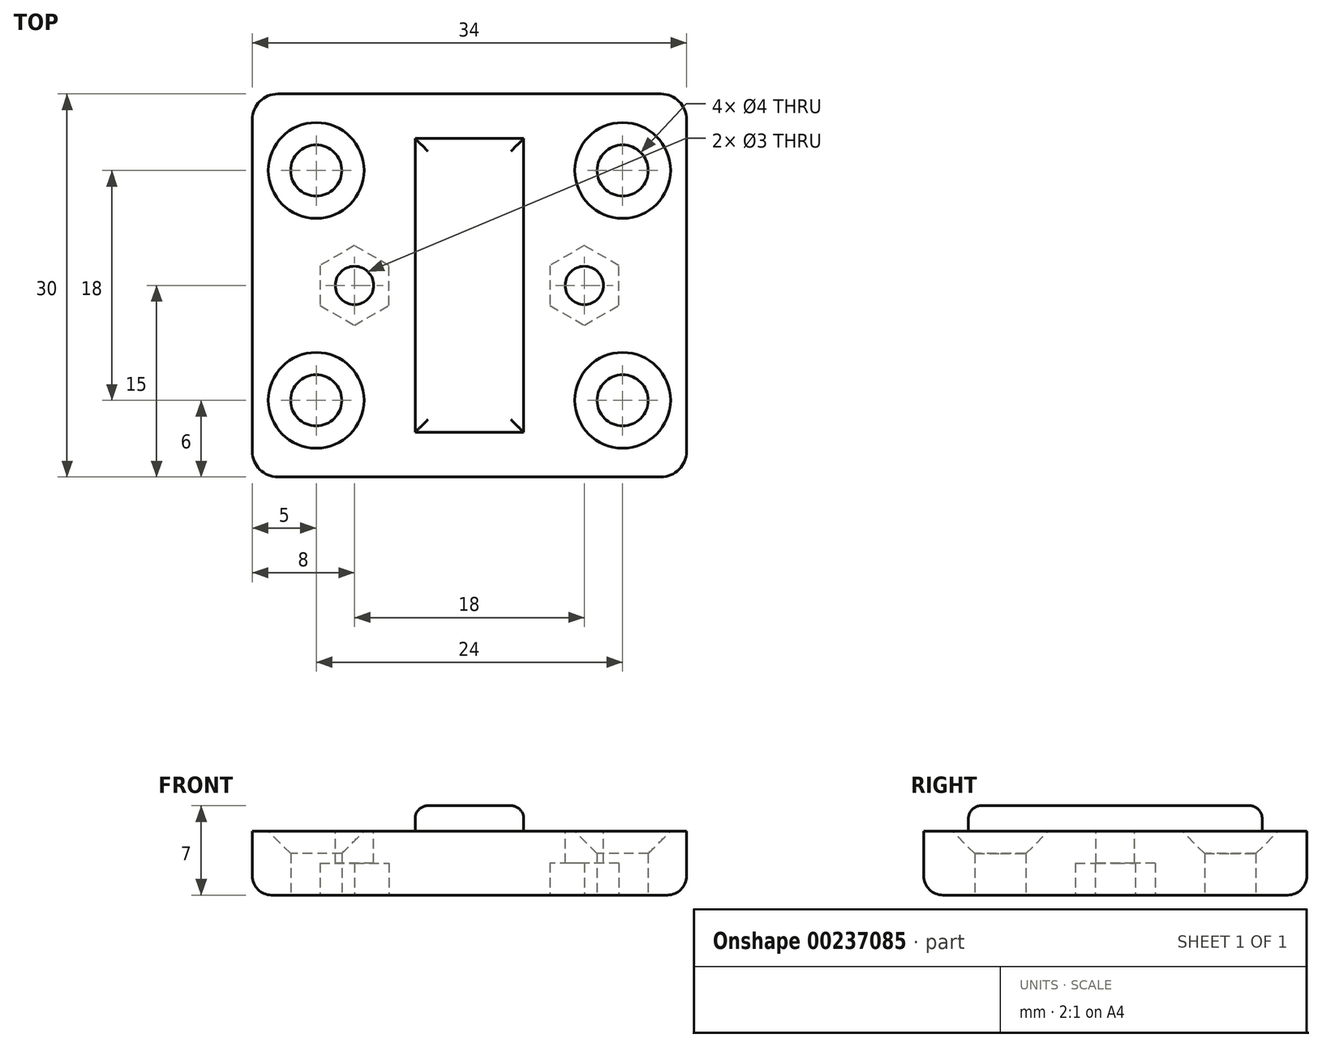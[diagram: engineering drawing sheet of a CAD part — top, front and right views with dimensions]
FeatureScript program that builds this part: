
annotation { "Feature Type Name" : "Feature", "Feature Type Description" : "" }
export const myFeature = defineFeature(function(context is Context, id is Id, definition is map)
    precondition{}
    {
        {
            var Q0;
            Q0=qCreatedBy(makeId("Top.planeOp"),FACE);
            var sketch = newSketch(context, id + "F0", { "sketchPlane" : qUnion([Q0])});
            skLineSegment(sketch, "E0.bottom", {"start": v(-12, 9) * mm, "end": v(12, 9) * mm, "construction": true});
            skLineSegment(sketch, "E0.top", {"start": v(-12, -9) * mm, "end": v(12, -9) * mm, "construction": true});
            skLineSegment(sketch, "E0.left", {"start": v(-12, 9) * mm, "end": v(-12, -9) * mm, "construction": true});
            skLineSegment(sketch, "E0.right", {"start": v(12, 9) * mm, "end": v(12, -9) * mm, "construction": true});
            skCircle(sketch, "E1", {"center": v(-12, 9) * mm, "radius": 2 * mm});
            skCircle(sketch, "E2", {"center": v(12, 9) * mm, "radius": 2 * mm});
            skCircle(sketch, "E3", {"center": v(-12, -9) * mm, "radius": 2 * mm});
            skCircle(sketch, "E4", {"center": v(12, -9) * mm, "radius": 2 * mm});
            skLineSegment(sketch, "E5.bottom", {"start": v(-17, -15) * mm, "end": v(17, -15) * mm});
            skLineSegment(sketch, "E5.top", {"start": v(-17, 15) * mm, "end": v(17, 15) * mm});
            skLineSegment(sketch, "E5.left", {"start": v(-17, -15) * mm, "end": v(-17, 15) * mm});
            skLineSegment(sketch, "E5.right", {"start": v(17, -15) * mm, "end": v(17, 15) * mm});
            skPoint(sketch, "E5.middle", {"position": v(0, 0) * mm});
            skSolve(sketch);
        }
        {
            var Q0;
            Q0=makeQuery(id+"F0.imprint","IMPRINT",FACE,{"disambiguationData":[TD([[makeQuery(id+"F0.imprint","IMPRINT",EDGE,{"derivedFrom":sQuery(id+"F0.wireOp",EDGE,"E1")}),-1.0]])]});
            var Q1;
            Q1=sQuery(id+"F0.wireOp",EDGE,"E0.right");
            var Q2;
            Q2=sQuery(id+"F0.wireOp",EDGE,"E0.bottom");
            var Q3;
            Q3=sQuery(id+"F0.wireOp",EDGE,"E0.left");
            var Q4;
            Q4=sQuery(id+"F0.wireOp",EDGE,"E0.top");
            extrude(context, id + "F1", {"entities" : qUnion([Q0]), "surfaceEntities" : qUnion([Q1, Q2, Q3, Q4]), "depth" : 5 * mm});
        }
        {
            var Q0;
            Q0=makeQuery(id+"F1.opExtrude","CAP_FACE",FACE,{"disambiguationData":[OSD([sQuery(id+"F0.wireOp",EDGE,"E1"),sQuery(id+"F0.wireOp",EDGE,"E2"),sQuery(id+"F0.wireOp",EDGE,"E3"),sQuery(id+"F0.wireOp",EDGE,"E4"),sQuery(id+"F0.wireOp",EDGE,"E5.bottom"),sQuery(id+"F0.wireOp",EDGE,"E5.top"),sQuery(id+"F0.wireOp",EDGE,"E5.left"),sQuery(id+"F0.wireOp",EDGE,"E5.right")])],"isStart":false});
            var sketch = newSketch(context, id + "F2", { "sketchPlane" : qUnion([Q0])});
            skLineSegment(sketch, "E6.bottom", {"start": v(15, 8) * mm, "end": v(9, 8) * mm, "construction": true});
            skLineSegment(sketch, "E6.top", {"start": v(15, -8) * mm, "end": v(9, -8) * mm, "construction": true});
            skLineSegment(sketch, "E6.left", {"start": v(15, 8) * mm, "end": v(15, -8) * mm, "construction": true});
            skLineSegment(sketch, "E6.right", {"start": v(9, 8) * mm, "end": v(9, -8) * mm, "construction": true});
            skCircle(sketch, "E7", {"center": v(15, 8) * mm, "radius": 1.5 * mm});
            skCircle(sketch, "E8", {"center": v(15, -8) * mm, "radius": 1.5 * mm});
            skCircle(sketch, "E9", {"center": v(15, 0) * mm, "radius": 1.5 * mm});
            skCircle(sketch, "E10", {"center": v(9, 8) * mm, "radius": 1.5 * mm});
            skCircle(sketch, "E11", {"center": v(9, 0) * mm, "radius": 1.5 * mm});
            skCircle(sketch, "E12", {"center": v(9, -8) * mm, "radius": 1.5 * mm});
            skLineSegment(sketch, "E13.bottom", {"start": v(-9, 8) * mm, "end": v(-15, 8) * mm, "construction": true});
            skLineSegment(sketch, "E13.top", {"start": v(-9, -8) * mm, "end": v(-15, -8) * mm, "construction": true});
            skLineSegment(sketch, "E13.left", {"start": v(-9, 8) * mm, "end": v(-9, -8) * mm, "construction": true});
            skLineSegment(sketch, "E13.right", {"start": v(-15, 8) * mm, "end": v(-15, -8) * mm, "construction": true});
            skLineSegment(sketch, "E14.bottom", {"start": v(12, -8) * mm, "end": v(-12, -8) * mm, "construction": true});
            skLineSegment(sketch, "E14.top", {"start": v(12, 8) * mm, "end": v(-12, 8) * mm, "construction": true});
            skLineSegment(sketch, "E14.left", {"start": v(12, -8) * mm, "end": v(12, 8) * mm, "construction": true});
            skLineSegment(sketch, "E14.right", {"start": v(-12, -8) * mm, "end": v(-12, 8) * mm, "construction": true});
            skPoint(sketch, "E14.middle", {"position": v(0, 0) * mm});
            skPoint(sketch, "E14.cornerSnap0", {"position": v(12, -8) * mm});
            skPoint(sketch, "E15", {"position": v(-12, -8) * mm});
            skCircle(sketch, "E16", {"center": v(-15, -8) * mm, "radius": 1.5 * mm});
            skCircle(sketch, "E17", {"center": v(-9, -8) * mm, "radius": 1.5 * mm});
            skCircle(sketch, "E18", {"center": v(-9, 8) * mm, "radius": 1.5 * mm});
            skCircle(sketch, "E19", {"center": v(-15, 8) * mm, "radius": 1.5 * mm});
            skCircle(sketch, "E20", {"center": v(-9, 0) * mm, "radius": 1.5 * mm});
            skCircle(sketch, "E21", {"center": v(-15, 0) * mm, "radius": 1.5 * mm});
            skPoint(sketch, "E22", {"position": v(12, 8) * mm});
            skPoint(sketch, "E23", {"position": v(-12, 8) * mm});
            skSolve(sketch);
        }
        {
            var Q0;
            Q0=makeQuery(id+"F2.imprint","IMPRINT",FACE,{"disambiguationData":[TD([[makeQuery(id+"F2.imprint","IMPRINT",EDGE,{"derivedFrom":sQuery(id+"F2.wireOp",EDGE,"E11")}),1.0]])]});
            var Q1;
            Q1=makeQuery(id+"F2.imprint","IMPRINT",FACE,{"disambiguationData":[TD([[makeQuery(id+"F2.imprint","IMPRINT",EDGE,{"derivedFrom":sQuery(id+"F2.wireOp",EDGE,"E20")}),1.0]])]});
            extrude(context, id + "F3", {"entities" : qUnion([Q0, Q1]), "operationType" : NewBodyOperationType.REMOVE, "endBound" : BoundingType.UP_TO_NEXT, "oppositeDirection" : true, "depth" : 25 * mm});
        }
        {
            var Q0;
            Q0=makeQuery(id+"F1.opExtrude","CAP_EDGE",EDGE,{"disambiguationData":[OSD([sQuery(id+"F0.wireOp",EDGE,"E3")])],"isStart":false});
            var Q1;
            Q1=makeQuery(id+"F1.opExtrude","CAP_EDGE",EDGE,{"disambiguationData":[OSD([sQuery(id+"F0.wireOp",EDGE,"E1")])],"isStart":false});
            var Q2;
            Q2=makeQuery(id+"F1.opExtrude","CAP_EDGE",EDGE,{"disambiguationData":[OSD([sQuery(id+"F0.wireOp",EDGE,"E2")])],"isStart":false});
            var Q3;
            Q3=makeQuery(id+"F1.opExtrude","CAP_EDGE",EDGE,{"disambiguationData":[OSD([sQuery(id+"F0.wireOp",EDGE,"E4")])],"isStart":false});
            chamfer(context, id + "F4", {"entities" : qUnion([Q0, Q1, Q2, Q3]), "width" : 1.75 * mm, "tangentPropagation" : true});
        }
        {
            var Q0;
            Q0=makeQuery(id+"F1.opExtrude","CAP_FACE",FACE,{"disambiguationData":[OSD([sQuery(id+"F0.wireOp",EDGE,"E1"),sQuery(id+"F0.wireOp",EDGE,"E2"),sQuery(id+"F0.wireOp",EDGE,"E3"),sQuery(id+"F0.wireOp",EDGE,"E4"),sQuery(id+"F0.wireOp",EDGE,"E5.bottom"),sQuery(id+"F0.wireOp",EDGE,"E5.top"),sQuery(id+"F0.wireOp",EDGE,"E5.left"),sQuery(id+"F0.wireOp",EDGE,"E5.right")])],"isStart":true});
            var sketch = newSketch(context, id + "F5", { "sketchPlane" : qUnion([Q0])});
            skCircle(sketch, "E24.cCircle", {"center": v(-9, 0) * mm, "radius": 2.7 * mm, "construction": true});
            skLineSegment(sketch, "E24.0", {"start": v(-6.3, 1.56) * mm, "end": v(-6.3, -1.56) * mm});
            skLineSegment(sketch, "E24.1", {"start": v(-6.3, -1.56) * mm, "end": v(-9, -3.12) * mm});
            skLineSegment(sketch, "E24.2", {"start": v(-9, -3.12) * mm, "end": v(-11.7, -1.56) * mm});
            skLineSegment(sketch, "E24.3", {"start": v(-11.7, -1.56) * mm, "end": v(-11.7, 1.56) * mm});
            skLineSegment(sketch, "E24.4", {"start": v(-11.7, 1.56) * mm, "end": v(-9, 3.12) * mm});
            skLineSegment(sketch, "E24.5", {"start": v(-9, 3.12) * mm, "end": v(-6.3, 1.56) * mm});
            skPoint(sketch, "E24.0.midPoint", {"position": v(-6.3, 0) * mm});
            skCircle(sketch, "E25.cCircle", {"center": v(9, 0) * mm, "radius": 2.7 * mm, "construction": true});
            skLineSegment(sketch, "E25.0", {"start": v(6.3, -1.56) * mm, "end": v(6.3, 1.56) * mm});
            skLineSegment(sketch, "E25.1", {"start": v(6.3, 1.56) * mm, "end": v(9, 3.12) * mm});
            skLineSegment(sketch, "E25.2", {"start": v(9, 3.12) * mm, "end": v(11.7, 1.56) * mm});
            skLineSegment(sketch, "E25.3", {"start": v(11.7, 1.56) * mm, "end": v(11.7, -1.56) * mm});
            skLineSegment(sketch, "E25.4", {"start": v(11.7, -1.56) * mm, "end": v(9, -3.12) * mm});
            skLineSegment(sketch, "E25.5", {"start": v(9, -3.12) * mm, "end": v(6.3, -1.56) * mm});
            skPoint(sketch, "E25.0.midPoint", {"position": v(6.3, 0) * mm});
            skLineSegment(sketch, "E26", {"start": v(-6.3, 0) * mm, "end": v(6.3, 0) * mm, "construction": true});
            skSolve(sketch);
        }
        {
            var Q0;
            Q0=makeQuery(id+"F5.imprint","IMPRINT",FACE,{"disambiguationData":[TD([[makeQuery(id+"F5.imprint","IMPRINT",EDGE,{"derivedFrom":sQuery(id+"F5.wireOp",EDGE,"E24.0")}),-1.0]])]});
            var Q1;
            Q1=makeQuery(id+"F5.imprint","IMPRINT",FACE,{"disambiguationData":[TD([[makeQuery(id+"F5.imprint","IMPRINT",EDGE,{"derivedFrom":sQuery(id+"F5.wireOp",EDGE,"E25.0")}),-1.0]])]});
            extrude(context, id + "F6", {"entities" : qUnion([Q0, Q1]), "operationType" : NewBodyOperationType.REMOVE, "oppositeDirection" : true, "depth" : 2.5 * mm});
        }
        {
            var Q0;
            Q0=makeQuery(id+"F1.opExtrude","CAP_FACE",FACE,{"disambiguationData":[OSD([sQuery(id+"F0.wireOp",EDGE,"E1"),sQuery(id+"F0.wireOp",EDGE,"E2"),sQuery(id+"F0.wireOp",EDGE,"E3"),sQuery(id+"F0.wireOp",EDGE,"E4"),sQuery(id+"F0.wireOp",EDGE,"E5.bottom"),sQuery(id+"F0.wireOp",EDGE,"E5.top"),sQuery(id+"F0.wireOp",EDGE,"E5.left"),sQuery(id+"F0.wireOp",EDGE,"E5.right")])],"isStart":false});
            var sketch = newSketch(context, id + "F7", { "sketchPlane" : qUnion([Q0])});
            skCircle(sketch, "E27.0", {"center": v(-12, 9) * mm, "radius": 3.75 * mm, "construction": true});
            skSolve(sketch);
        }
        {
            var Q0;
            Q0=makeQuery(id+"F1.opExtrude","SWEPT_EDGE",EDGE,{"disambiguationData":[OSD([sQuery(id+"F0.wireOp",EDGE,"E5.bottom"),sQuery(id+"F0.wireOp",EDGE,"E5.right")])]});
            var Q1;
            Q1=makeQuery(id+"F1.opExtrude","SWEPT_EDGE",EDGE,{"disambiguationData":[OSD([sQuery(id+"F0.wireOp",EDGE,"E5.top"),sQuery(id+"F0.wireOp",EDGE,"E5.right")])]});
            var Q2;
            Q2=makeQuery(id+"F1.opExtrude","SWEPT_EDGE",EDGE,{"disambiguationData":[OSD([sQuery(id+"F0.wireOp",EDGE,"E5.bottom"),sQuery(id+"F0.wireOp",EDGE,"E5.left")])]});
            var Q3;
            Q3=makeQuery(id+"F1.opExtrude","SWEPT_EDGE",EDGE,{"disambiguationData":[OSD([sQuery(id+"F0.wireOp",EDGE,"E5.top"),sQuery(id+"F0.wireOp",EDGE,"E5.left")])]});
            fillet(context, id + "F8", {"entities" : qUnion([Q0, Q1, Q2, Q3]), "radius" : 2 * mm, "tangentPropagation" : true, "allowEdgeOverflow" : false});
        }
        {
            var Q0;
            Q0=makeQuery(id+"F1.opExtrude","CAP_EDGE",EDGE,{"disambiguationData":[OSD([sQuery(id+"F0.wireOp",EDGE,"E5.bottom")])],"isStart":true});
            fillet(context, id + "F9", {"entities" : qUnion([Q0]), "radius" : 1.5 * mm, "tangentPropagation" : true, "allowEdgeOverflow" : false});
        }
        {
            var Q0;
            {var subQ3=sQuery(id+"F0.wireOp",EDGE,"E5.bottom");Q0=makeQuery(id+"F7.imprint","IMPRINT",FACE,{"disambiguationData":[TD([[makeQuery(id+"F7.imprint","IMPRINT",EDGE,{"derivedFrom":makeQuery(id+"F1.opExtrude","CAP_EDGE",EDGE,{"disambiguationData":[OSD([subQ3])],"isStart":false})}),1.0]])]});}
            var sketch = newSketch(context, id + "F10", { "sketchPlane" : qUnion([Q0])});
            skLineSegment(sketch, "E28.bottom", {"start": v(4.25, -11.5) * mm, "end": v(-4.25, -11.5) * mm});
            skLineSegment(sketch, "E28.top", {"start": v(4.25, 11.5) * mm, "end": v(-4.25, 11.5) * mm});
            skLineSegment(sketch, "E28.left", {"start": v(4.25, -11.5) * mm, "end": v(4.25, 11.5) * mm});
            skLineSegment(sketch, "E28.right", {"start": v(-4.25, -11.5) * mm, "end": v(-4.25, 11.5) * mm});
            skPoint(sketch, "E28.middle", {"position": v(0, 0) * mm});
            skSolve(sketch);
        }
        {
            var Q0;
            Q0 = qSketchRegion(id + "F10", true);
            extrude(context, id + "F11", {"entities" : qUnion([Q0]), "operationType" : NewBodyOperationType.ADD, "depth" : 2 * mm});
        }
        {
            var Q0;
            Q0=makeQuery(id+"F11.opExtrude","CAP_EDGE",EDGE,{"disambiguationData":[OSD([sQuery(id+"F10.wireOp",EDGE,"E28.bottom")])],"isStart":false});
            var Q1;
            Q1=makeQuery(id+"F11.opExtrude","CAP_EDGE",EDGE,{"disambiguationData":[OSD([sQuery(id+"F10.wireOp",EDGE,"E28.left")])],"isStart":false});
            var Q2;
            Q2=makeQuery(id+"F11.opExtrude","CAP_EDGE",EDGE,{"disambiguationData":[OSD([sQuery(id+"F10.wireOp",EDGE,"E28.right")])],"isStart":false});
            var Q3;
            Q3=makeQuery(id+"F11.opExtrude","CAP_EDGE",EDGE,{"disambiguationData":[OSD([sQuery(id+"F10.wireOp",EDGE,"E28.top")])],"isStart":false});
            fillet(context, id + "F12", {"entities" : qUnion([Q0, Q1, Q2, Q3]), "radius" : 1 * mm, "tangentPropagation" : true, "allowEdgeOverflow" : false});
        }
    });
